# Revit family: ERA-RA25
name_source: partatom
category: Lighting Fixtures
revit_build: Autodesk Revit 2014 (Build: 20130308_1515(x64)
units: mm (PartAtom-declared; Revit-internal decimal feet)

## types (4) — shared parameters
1 = Yes
Angle Bee = 180.00°
Apparent Load = 68 VA
Arm Material = Metal-Kim Lighting-Aluminum Alloy
Assembly Code = D5020200
Description = Site/Roadway Luminaire
Finish = All colors shall be a Super TGIC powder coat paint. Optional white (WH) and custom colors available.
Glass Material = Glass-Kim Lighting-Clear
Height = 17 1/2"
Housing Material = Metal-Kim Lighting-Aluminum Alloy
Inside Material = Metal-Kim Lighting-Aluminum-Reflective
Lamp = LED
Load Classification = Lighting
Manufacturer = Kim Lighting
MasterFormat Title = Parking Lighting, Roadway Lighting, Site Lighting
Model = Era
Mount Height = 192"
Number of Poles = 1
Photometric Notes = More IES files download on Photometric Web Link
Photometric Web Link = https://www.hubbell.com
Pole Finish = Metal-Kim Lighting-Aluminum Alloy
Pole Height = 175 1/2"
Power Factor = 1
Product Documentation Link = http://www.kimlighting.com
Product Page URL = http://www.kimlighting.com
Series = ERA LUMINAIRE
Type Comments = Lighting Fixture
URL = http://www.kimlighting.com
Voltage = 120 V
Wattage Comments = 60 LEDs, 68 W

## per-type parameters (varying)
| type | 2 | 3Y | 4C |
| ER-RA17-1A | No | No | No |
| ER-RA17-2B | Yes | No | No |
| ER-RA17-3Y | No | Yes | No |
| ER-RA17-4C | Yes | No | Yes |

## geometry (parser evidence)
native form markers: Blend x8, Sweep x6
no freeform markers — native parametric forms only
